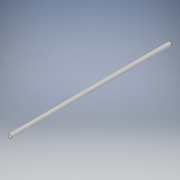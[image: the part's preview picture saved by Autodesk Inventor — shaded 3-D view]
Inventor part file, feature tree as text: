
AUTODESK INVENTOR PART (.ipt)
format: ipt  version: 2019 (Build 230136000, 136)  size: 90,112 bytes
history: native  units: mm
features: extrude x1, sketch x1
ambient origin geometry x8: Origin, YZ Plane, XZ Plane, XY Plane, X Axis, Y Axis, Z Axis, Center Point
bodies: Solid1 (feature_tree)
feature tree (2):
  extrude  "Extrusion1"  Depth=635.0mm TaperAngle=0.0deg
  sketch  "Sketch1"  dims[d0=15.0mm d1=635.0mm d2=0.0mm]
